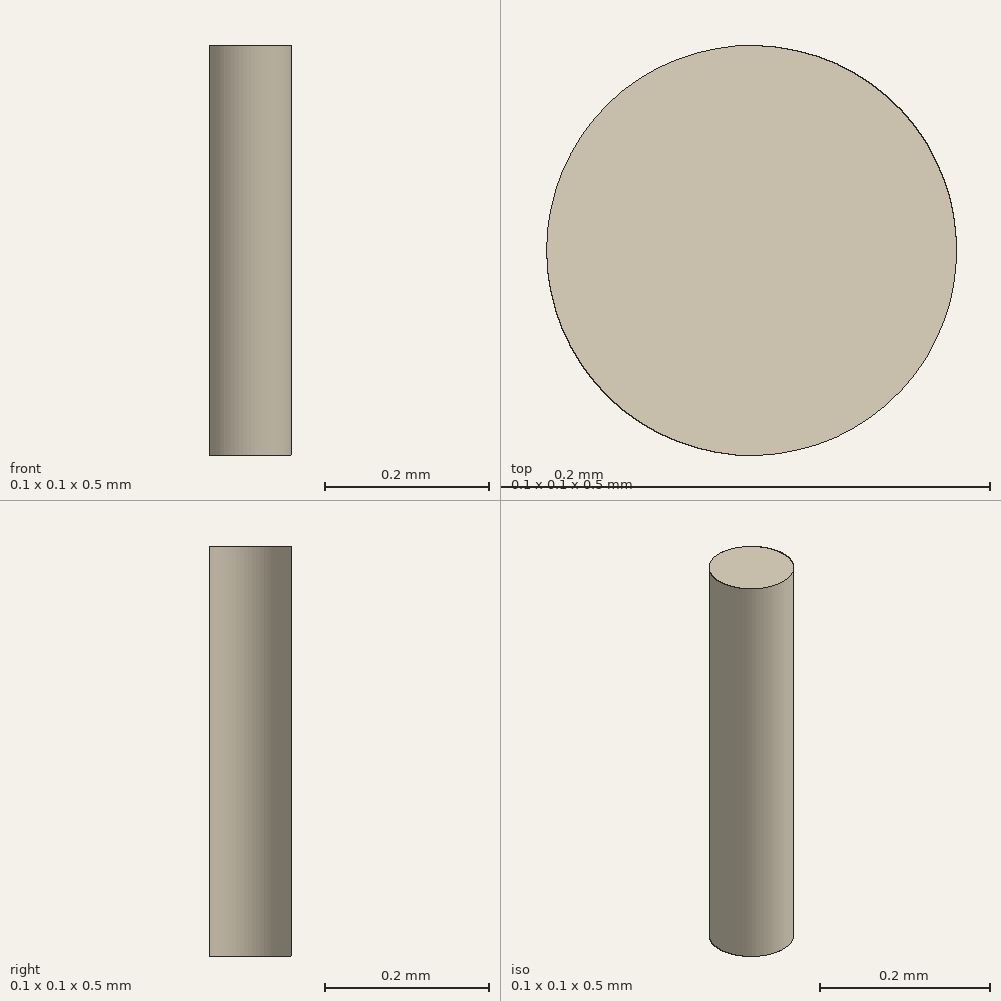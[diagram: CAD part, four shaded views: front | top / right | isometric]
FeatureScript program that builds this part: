
annotation { "Feature Type Name" : "Feature", "Feature Type Description" : "" }
export const myFeature = defineFeature(function(context is Context, id is Id, definition is map)
    precondition{}
    {
        {
            var Q0;
            Q0=qCreatedBy(makeId("Front.planeOp"),FACE);
            var sketch = newSketch(context, id + "F0", { "sketchPlane" : qUnion([Q0])});
            skLineSegment(sketch, "E0.bottom", {"start": v(0, 0) * mm, "end": v(-0.05, 0) * mm});
            skLineSegment(sketch, "E0.top", {"start": v(0, 0.5) * mm, "end": v(-0.05, 0.5) * mm});
            skLineSegment(sketch, "E0.left", {"start": v(0, 0) * mm, "end": v(0, 0.5) * mm});
            skLineSegment(sketch, "E0.right", {"start": v(-0.05, 0) * mm, "end": v(-0.05, 0.5) * mm});
            skSolve(sketch);
        }
        {
            var Q0;
            Q0=makeQuery(id+"F0.imprint","IMPRINT",FACE,{"disambiguationData":[TD([[makeQuery(id+"F0.imprint","IMPRINT",EDGE,{"derivedFrom":sQuery(id+"F0.wireOp",EDGE,"E0.bottom")}),-1.0]])]});
            var Q1;
            Q1=sQuery(id+"F0.wireOp",EDGE,"E0.left");
            revolve(context, id + "F1", {"surfaceOperationType" : NewSurfaceOperationType.NEW, "entities" : qUnion([Q0]), "axis" : qUnion([Q1]), "revolveType" : RevolveType.FULL});
        }
    });
